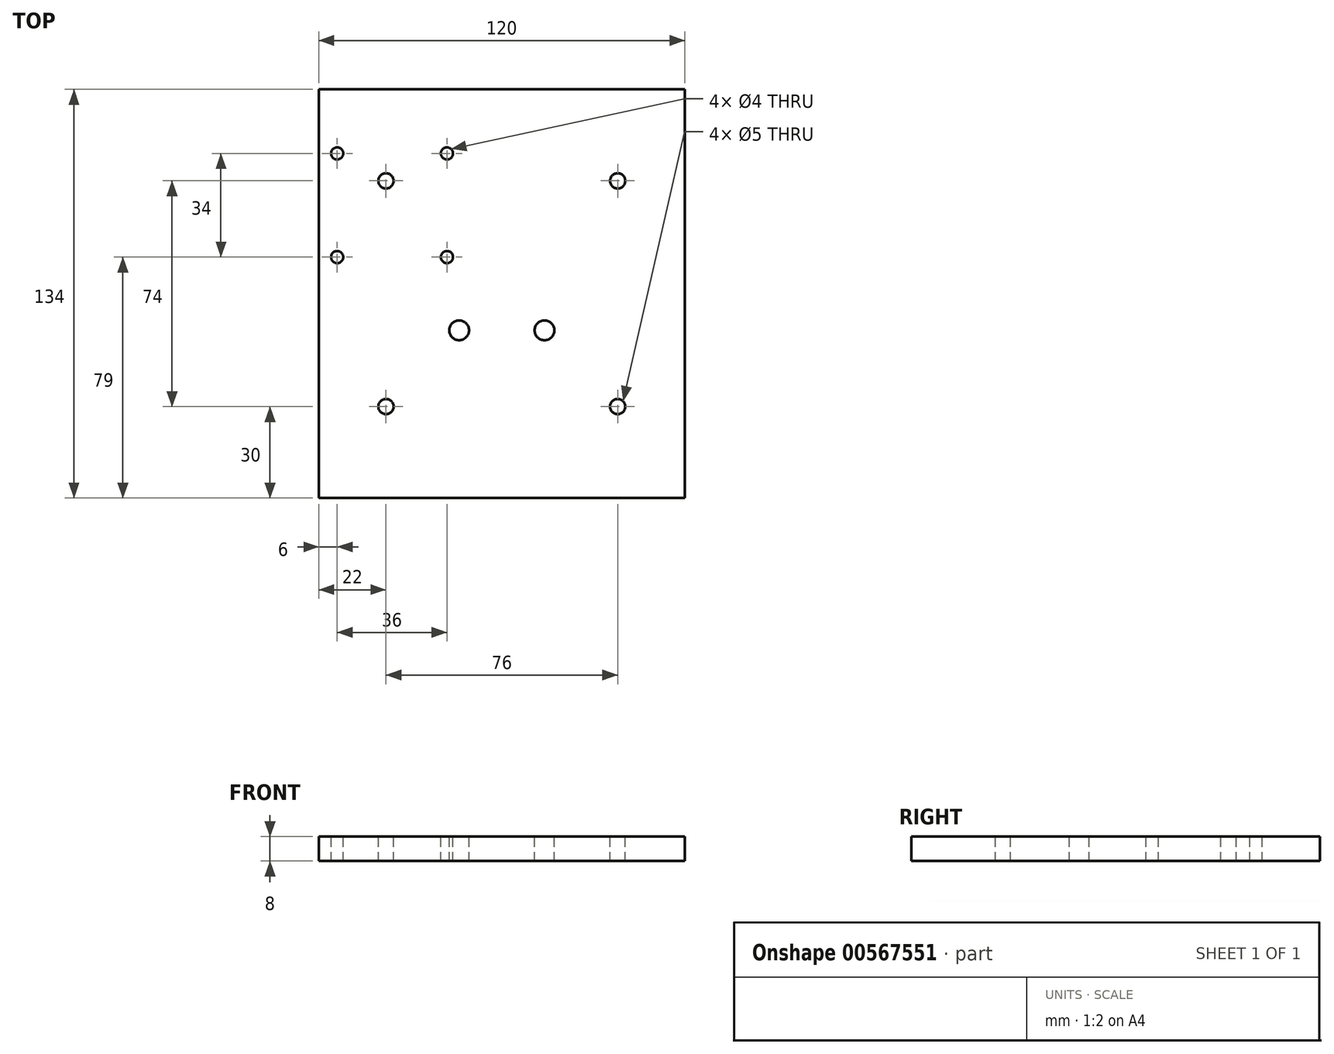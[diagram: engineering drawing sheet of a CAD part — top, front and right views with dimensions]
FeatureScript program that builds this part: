
annotation { "Feature Type Name" : "Feature", "Feature Type Description" : "" }
export const myFeature = defineFeature(function(context is Context, id is Id, definition is map)
    precondition{}
    {
        {
            var Q0;
            Q0=qCreatedBy(makeId("Top.planeOp"),FACE);
            var sketch = newSketch(context, id + "F0", { "sketchPlane" : qUnion([Q0])});
            skLineSegment(sketch, "E0.bottom", {"start": v(60, -75) * mm, "end": v(-60, -75) * mm});
            skLineSegment(sketch, "E0.top", {"start": v(60, 75) * mm, "end": v(-60, 75) * mm});
            skLineSegment(sketch, "E0.left", {"start": v(60, -75) * mm, "end": v(60, 75) * mm});
            skLineSegment(sketch, "E0.right", {"start": v(-60, -75) * mm, "end": v(-60, 75) * mm});
            skPoint(sketch, "E0.middle", {"position": v(0, 0) * mm});
            skSolve(sketch);
        }
        {
            var Q0;
            Q0 = qSketchRegion(id + "F0", true);
            extrude(context, id + "F1", {"entities" : qUnion([Q0]), "depth" : 8 * mm, "offsetDistance" : 25 * mm});
        }
        {
            var Q0;
            Q0=makeQuery(id+"F1.opExtrude","CAP_FACE",FACE,{"disambiguationData":[OSD([sQuery(id+"F0.wireOp",EDGE,"E0.bottom"),sQuery(id+"F0.wireOp",EDGE,"E0.top"),sQuery(id+"F0.wireOp",EDGE,"E0.left"),sQuery(id+"F0.wireOp",EDGE,"E0.right")])],"isStart":false});
            var sketch = newSketch(context, id + "F2", { "sketchPlane" : qUnion([Q0])});
            skCircle(sketch, "E1", {"center": v(-54, 54) * mm, "radius": 2 * mm});
            skCircle(sketch, "E2", {"center": v(-18, 54) * mm, "radius": 2 * mm});
            skCircle(sketch, "E3", {"center": v(-18, 20) * mm, "radius": 2 * mm});
            skCircle(sketch, "E4", {"center": v(-54, 20) * mm, "radius": 2 * mm});
            skSolve(sketch);
        }
        {
            var Q0;
            Q0 = qSketchRegion(id + "F2", true);
            extrude(context, id + "F3", {"entities" : qUnion([Q0]), "operationType" : NewBodyOperationType.REMOVE, "endBound" : BoundingType.UP_TO_NEXT, "oppositeDirection" : true, "depth" : 25 * mm, "offsetDistance" : 25 * mm});
        }
        {
            var Q0;
            Q0=makeQuery(id+"F1.opExtrude","CAP_FACE",FACE,{"disambiguationData":[OSD([sQuery(id+"F0.wireOp",EDGE,"E0.bottom"),sQuery(id+"F0.wireOp",EDGE,"E0.top"),sQuery(id+"F0.wireOp",EDGE,"E0.left"),sQuery(id+"F0.wireOp",EDGE,"E0.right")])],"isStart":false});
            var sketch = newSketch(context, id + "F4", { "sketchPlane" : qUnion([Q0])});
            skCircle(sketch, "E5", {"center": v(-14, -4) * mm, "radius": 3.25 * mm});
            skCircle(sketch, "E6", {"center": v(14, -4) * mm, "radius": 3.25 * mm});
            skLineSegment(sketch, "E7.bottom", {"start": v(-60, -75) * mm, "end": v(60, -75) * mm});
            skLineSegment(sketch, "E7.top", {"start": v(-60, -59) * mm, "end": v(60, -59) * mm});
            skLineSegment(sketch, "E7.left", {"start": v(-60, -75) * mm, "end": v(-60, -59) * mm});
            skLineSegment(sketch, "E7.right", {"start": v(60, -75) * mm, "end": v(60, -59) * mm});
            skCircle(sketch, "E8", {"center": v(38, -29) * mm, "radius": 2.5 * mm});
            skCircle(sketch, "E9", {"center": v(38, 45) * mm, "radius": 2.5 * mm});
            skCircle(sketch, "E10", {"center": v(-38, 45) * mm, "radius": 2.5 * mm});
            skCircle(sketch, "E11", {"center": v(-38, -29) * mm, "radius": 2.5 * mm});
            skSolve(sketch);
        }
        {
            var Q0;
            Q0 = qSketchRegion(id + "F4", true);
            extrude(context, id + "F5", {"entities" : qUnion([Q0]), "operationType" : NewBodyOperationType.REMOVE, "endBound" : BoundingType.UP_TO_NEXT, "oppositeDirection" : true, "depth" : 25 * mm, "offsetDistance" : 25 * mm});
        }
    });
